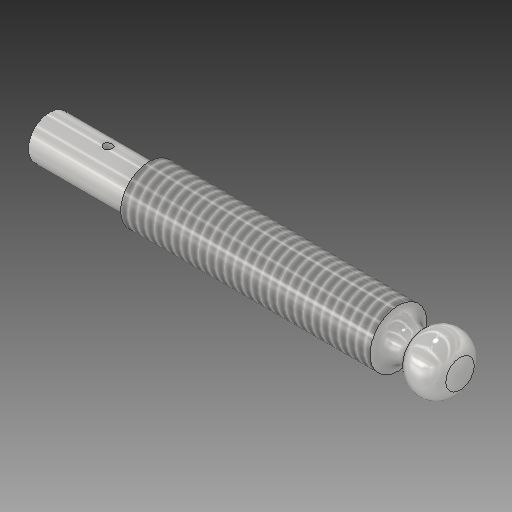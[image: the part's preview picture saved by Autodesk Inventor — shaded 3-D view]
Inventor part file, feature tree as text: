
AUTODESK INVENTOR PART (.ipt)
format: ipt  version: 2020 (Build 240168000, 168)  size: 206,336 bytes
history: native  units: in
note: dims shown in document units (in); Inventor stores cm internally (conversion verified against a paired STEP export)
features: sketch x2, revolve x1, thread x1, plane x1, hole x1, other x1
ambient origin geometry x8: Origin, YZ Plane, XZ Plane, XY Plane, X Axis, Y Axis, Z Axis, Center Point
bodies: Solid1 (feature_tree)
feature tree (7):
  revolve  "Revolution1"  [1 undecoded]
  thread  "Thread1"  [1 undecoded]
  plane  "Work Plane1"
  hole  "Hole1"  [1 undecoded]
  sketch  "Sketch1"  dims[d0=3.625in d1=0.0in d2=0.875in]
  other  "Work Point1"
  sketch  "Sketch2"  dims[d3=2.1875in d4=0.373in d5=0.5in d6=0.5in d12=0.1875in d13=0.1875in d14=0.125in d15=0.375in d16=90.0deg d17=1.0in d18=0.0in d19=0.075in d20=0.75in d21=0.375in d22=0.25in d23=0.5635in d24=1.0in d25=0.8108in]
note: 3 required parameter values undecoded (feature->parameter linkage not recoverable at this tier; creation-order binding heuristic only, values carry confidence <= 0.55)